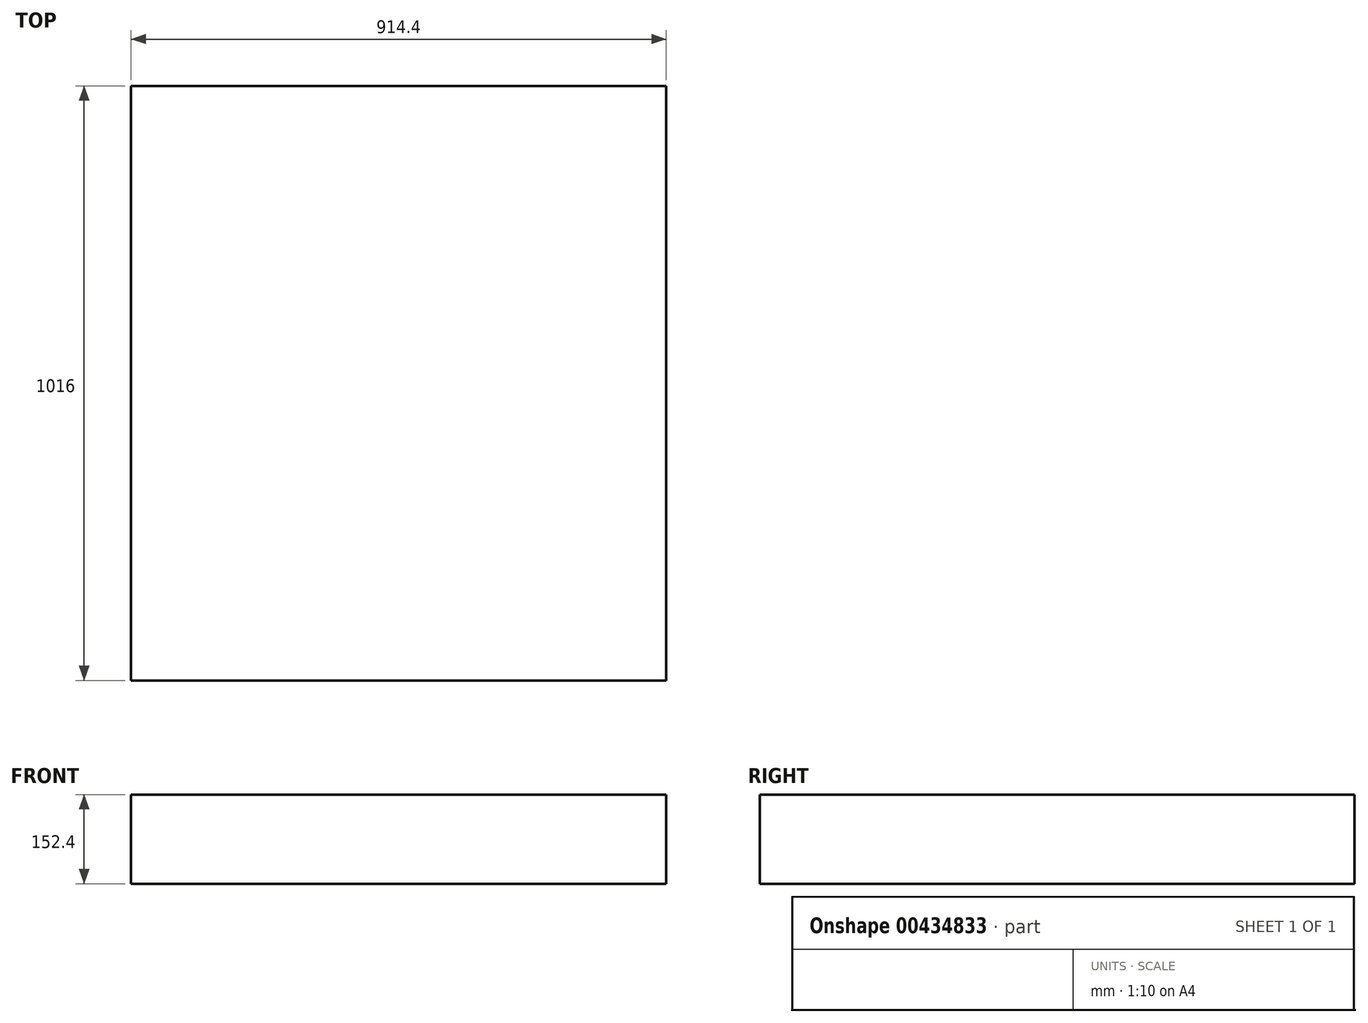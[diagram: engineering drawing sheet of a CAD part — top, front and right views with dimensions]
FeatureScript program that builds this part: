
annotation { "Feature Type Name" : "Feature", "Feature Type Description" : "" }
export const myFeature = defineFeature(function(context is Context, id is Id, definition is map)
    precondition{}
    {
        {
            var Q0;
            Q0=qCreatedBy(makeId("Top.planeOp"),FACE);
            var sketch = newSketch(context, id + "F0", { "sketchPlane" : qUnion([Q0])});
            skLineSegment(sketch, "E0.bottom", {"start": v(-80.94, -50.31) * mm, "end": v(833.46, -50.31) * mm});
            skLineSegment(sketch, "E0.top", {"start": v(-80.94, 965.69) * mm, "end": v(833.46, 965.69) * mm});
            skLineSegment(sketch, "E0.left", {"start": v(-80.94, -50.31) * mm, "end": v(-80.94, 965.69) * mm});
            skLineSegment(sketch, "E0.right", {"start": v(833.46, -50.31) * mm, "end": v(833.46, 965.69) * mm});
            skSolve(sketch);
        }
        {
            var Q0;
            Q0 = qSketchRegion(id + "F0", true);
            extrude(context, id + "F1", {"entities" : qUnion([Q0]), "depth" : 152.4 * mm});
        }
    });
